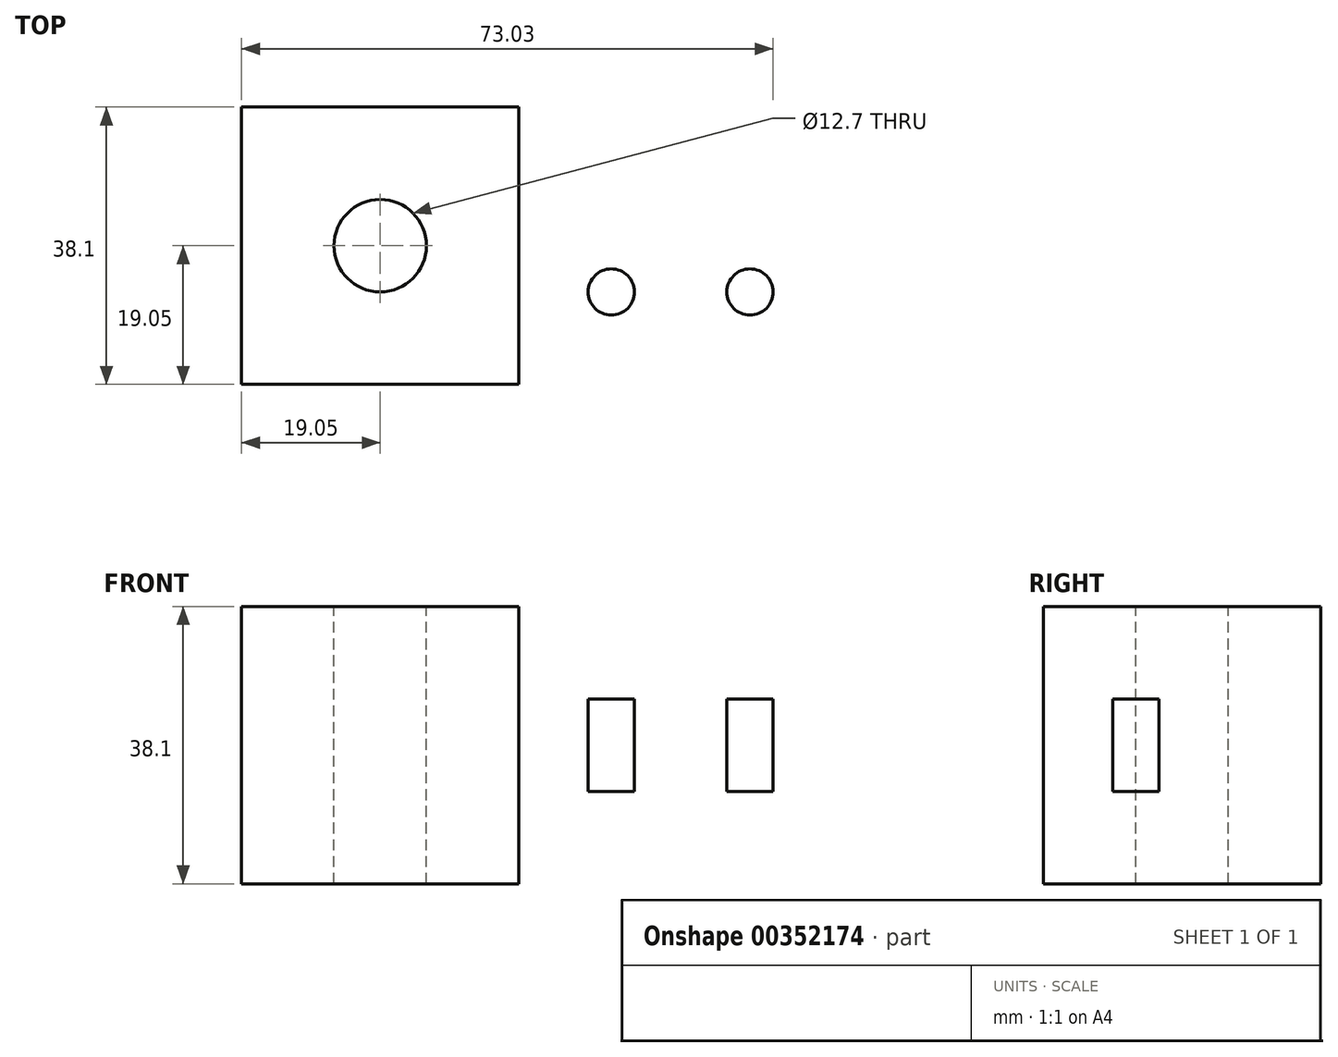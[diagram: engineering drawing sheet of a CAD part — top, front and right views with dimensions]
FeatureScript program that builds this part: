
annotation { "Feature Type Name" : "Feature", "Feature Type Description" : "" }
export const myFeature = defineFeature(function(context is Context, id is Id, definition is map)
    precondition{}
    {
        {
            var Q0;
            Q0=qCreatedBy(makeId("Front.planeOp"),FACE);
            var sketch = newSketch(context, id + "F0", { "sketchPlane" : qUnion([Q0])});
            skLineSegment(sketch, "E0", {"start": v(0, 0) * mm, "end": v(0, 38.1) * mm});
            skLineSegment(sketch, "E1", {"start": v(0, 38.1) * mm, "end": v(38.1, 38.1) * mm});
            skLineSegment(sketch, "E2", {"start": v(38.1, 38.1) * mm, "end": v(38.1, 25.4) * mm});
            skLineSegment(sketch, "E3", {"start": v(38.1, 25.4) * mm, "end": v(88.9, 25.4) * mm});
            skLineSegment(sketch, "E4", {"start": v(88.9, 25.4) * mm, "end": v(88.9, 12.7) * mm});
            skLineSegment(sketch, "E5", {"start": v(88.9, 12.7) * mm, "end": v(38.1, 12.7) * mm});
            skLineSegment(sketch, "E6", {"start": v(38.1, 12.7) * mm, "end": v(38.1, 0) * mm});
            skLineSegment(sketch, "E7", {"start": v(38.1, 0) * mm, "end": v(0, 0) * mm});
            skSolve(sketch);
        }
        {
            var Q0;
            Q0=makeQuery(id+"F0.imprint","IMPRINT",FACE,{"disambiguationData":[TD([[makeQuery(id+"F0.imprint","IMPRINT",EDGE,{"derivedFrom":sQuery(id+"F0.wireOp",EDGE,"E0")}),-1.0]])]});
            extrude(context, id + "F1", {"entities" : qUnion([Q0]), "depth" : 38.1 * mm});
        }
        {
            var Q0;
            Q0=makeQuery(id+"F1.opExtrude","SWEPT_FACE",FACE,{"disambiguationData":[OSD([sQuery(id+"F0.wireOp",EDGE,"E3")])]});
            var sketch = newSketch(context, id + "F2", { "sketchPlane" : qUnion([Q0])});
            skLineSegment(sketch, "E8", {"start": v(38.1, -19.05) * mm, "end": v(96.75, -19.05) * mm, "construction": true});
            skArc(sketch, "E9", {"start": v(69.85, -38.1) * mm, "mid": v(88.9, -19.05) * mm, "end": v(69.85, 0) * mm});
            skCircle(sketch, "E10", {"center": v(50.8, -12.7) * mm, "radius": 3.18 * mm});
            skCircle(sketch, "E11", {"center": v(69.85, -12.7) * mm, "radius": 3.18 * mm});
            skCircle(sketch, "E12.MirrorC", {"center": v(69.85, -25.4) * mm, "radius": 3.18 * mm});
            skCircle(sketch, "E13.MirrorC", {"center": v(50.8, -25.4) * mm, "radius": 3.18 * mm});
            skSolve(sketch);
        }
        {
            var Q0;
            {var subQ0=sQuery(id+"F2.wireOp",EDGE,"E9");var subQ1=sQuery(id+"F0.wireOp",EDGE,"E3");var subQ2=makeQuery(id+"F1.opExtrude","CAP_EDGE",EDGE,{"disambiguationData":[OSD([subQ1])],"isStart":true});var subQ3=makeQuery(id+"F2.imprint","INTERSECT",VERTEX,{"derivedFrom":[subQ2,subQ0]});Q0=makeQuery(id+"F2.imprint","IMPRINT",FACE,{"disambiguationData":[TD([[makeQuery(id+"F2.imprint","IMPRINT",EDGE,{"disambiguationData":[TD([[subQ3,1.0]])],"derivedFrom":subQ0}),-1.0]])]});}
            var Q1;
            {var subQ0=sQuery(id+"F2.wireOp",EDGE,"E9");var subQ1=sQuery(id+"F0.wireOp",EDGE,"E3");var subQ2=makeQuery(id+"F1.opExtrude","CAP_EDGE",EDGE,{"disambiguationData":[OSD([subQ1])],"isStart":false});var subQ3=makeQuery(id+"F2.imprint","INTERSECT",VERTEX,{"derivedFrom":[subQ2,subQ0]});Q1=makeQuery(id+"F2.imprint","IMPRINT",FACE,{"disambiguationData":[TD([[makeQuery(id+"F2.imprint","IMPRINT",EDGE,{"disambiguationData":[TD([[subQ3,-1.0]])],"derivedFrom":subQ0}),-1.0]])]});}
            extrude(context, id + "F3", {"entities" : qUnion([Q0, Q1]), "operationType" : NewBodyOperationType.REMOVE, "oppositeDirection" : true, "depth" : 25.4 * mm});
        }
        {
            var Q0;
            Q0=makeQuery(id+"F2.imprint","IMPRINT",FACE,{"disambiguationData":[TD([[makeQuery(id+"F2.imprint","IMPRINT",EDGE,{"derivedFrom":sQuery(id+"F2.wireOp",EDGE,"E10")}),1.0]])]});
            var Q1;
            Q1=makeQuery(id+"F2.imprint","IMPRINT",FACE,{"disambiguationData":[TD([[makeQuery(id+"F2.imprint","IMPRINT",EDGE,{"derivedFrom":sQuery(id+"F2.wireOp",EDGE,"E11")}),1.0]])]});
            var Q2;
            Q2=makeQuery(id+"F2.imprint","IMPRINT",FACE,{"disambiguationData":[TD([[makeQuery(id+"F2.imprint","IMPRINT",EDGE,{"derivedFrom":sQuery(id+"F2.wireOp",EDGE,"E12.MirrorC")}),-1.0]])]});
            var Q3;
            Q3=makeQuery(id+"F2.imprint","IMPRINT",FACE,{"disambiguationData":[TD([[makeQuery(id+"F2.imprint","IMPRINT",EDGE,{"derivedFrom":sQuery(id+"F2.wireOp",EDGE,"E13.MirrorC")}),-1.0]])]});
            extrude(context, id + "F4", {"entities" : qUnion([Q0, Q1, Q2, Q3]), "operationType" : NewBodyOperationType.REMOVE, "endBound" : BoundingType.THROUGH_ALL, "oppositeDirection" : true, "depth" : 25.4 * mm});
        }
        {
            var Q0;
            Q0=makeQuery(id+"F1.opExtrude","SWEPT_FACE",FACE,{"disambiguationData":[OSD([sQuery(id+"F0.wireOp",EDGE,"E1")])]});
            var sketch = newSketch(context, id + "F5", { "sketchPlane" : qUnion([Q0])});
            skLineSegment(sketch, "E14", {"start": v(0, -19.05) * mm, "end": v(38.1, -19.05) * mm, "construction": true});
            skLineSegment(sketch, "E15", {"start": v(19.05, 0) * mm, "end": v(19.05, -38.1) * mm, "construction": true});
            skCircle(sketch, "E16", {"center": v(19.05, -19.05) * mm, "radius": 6.35 * mm});
            skSolve(sketch);
        }
        {
            var Q0;
            Q0=makeQuery(id+"F5.imprint","IMPRINT",FACE,{"disambiguationData":[TD([[makeQuery(id+"F5.imprint","IMPRINT",EDGE,{"derivedFrom":sQuery(id+"F5.wireOp",EDGE,"E16")}),1.0]])]});
            extrude(context, id + "F6", {"entities" : qUnion([Q0]), "operationType" : NewBodyOperationType.REMOVE, "endBound" : BoundingType.THROUGH_ALL, "oppositeDirection" : true, "depth" : 25.4 * mm});
        }
    });
